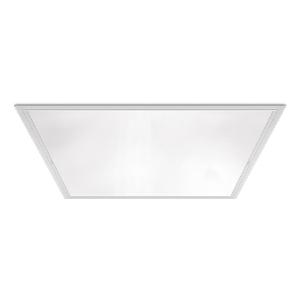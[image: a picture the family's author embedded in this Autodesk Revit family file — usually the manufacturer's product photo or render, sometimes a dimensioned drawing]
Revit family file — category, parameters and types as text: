
# Revit family: 3f_filippi_-_l_340_luce_diffusa_lgs_ip65v_3f_filippi_-_23972_-_l_340_25w-840_lgs_ip65v_596x596
name_source: partatom
category: Lighting Fixtures
units: mm (PartAtom-declared; Revit-internal decimal feet)

## family parameters
Cut with Voids When Loaded = No
Host = Face
Light Source = No
Part Type = Normal
Room Calculation Point = No
Round Connector Dimension = Use Diameter
Shared = No

## types (1)
- 3F Filippi - L 340 Luce Diffusa LGS IP65V (1 x LED, 3785 lm, 29 W, 4000 K)
    Apparent Load = 29 VA
    Approval mark = ENEC
    CIE Flux Codes = 67 92 98 100 100
    Color Rendering = 80
    Color Temperature = 4000 K
    Control Gear = Electronic ballast
    Default Elevation = 1800 mm
    Description = ILLUMINOTECHNICAL
Luminous efficiency 100% (DLOR 100%, ULOR 0%).
Initial luminous flux of the luminaire 3785 lm.
Direct symmetric distribution.
Installation Interdistance Transv.D = 1.19 x hu - Long.D = 1.17 x hu.
Average luminance <1500 cd/m² for radial angles >65°.
Tabular UGR (CIE 117 - 4H-8H; S=0.25H; 70/50/20): RUG 16.4 - 16.4.
Beam angle: 87° - 86°.
Luminous efficacy 131 lm/W.
Lifetime (L93/B10): 30000 h. (tq+25°C)
Lifetime (L90/B10): 50000 h. (tq+25°C)
Lifetime (L85/B10): 80000 h. (tq+25°C)
Lifetime (L80/B10): 100000 h. (tq+25°C)
Sudden decreased luminous flux after 50000 hours: 0% (C0).
Photobiological safety in compliance with IEC/TR 62778: RG0 risk exempt, (IEC 62471).
In compliance with IEC/EN 62722-2-1 - IEC/EN 62717 standards.

SOURCE
Squared LED module 25W/840.
Energy efficiency class (UE 2019/2020 - UE 2019/2015): C.
CIE 13.3 Colour rendering index: CRI >80 (R9 <50%).
IES TM-30 Fidelity Index: Rf = 84 Rg = 95.
CCT nominal colour temperature 4000 K.
Colour initial tolerance (MacAdam): SDCM 3.

MECHANICAL
Housing in hot-galvanised steel, painted in white polyester.
Perimetral frame in white polycarbonate.
LGS micro-prismatic flat diffuser in transparent methacrylate (PMMA), multi-lenticular exterior, anti-glare.
Anti-glare opal polycarbonate filter for brightness uniformity.
Luminaire with limited surface temperature. - D - (EN 60598-2-24)
Dimensions: 596x596 mm, height 80 mm. Weight 4.45 kg.
IP65 protection degree for exposed part, IP40 for recessed part.
Mechanical strength to impacts IK06 (1 joule).
Glow-wire test resistance 650°C.

ELECTRICAL
Wiring on a separate unit.
Halogen Free electronic wiring 230V-50/60Hz, power factor 0.95, THD <25%, constant output current, SELV, class II, 1 driver.
Power of the luminaire 29 W.
CE - IEC 60598-1 - EN 60598-1.
SAFE FLICKER: PstLM=<1 and SVM=<0.4 (IEC TR 61547-1 and IEC TR 63158), to ensure a more comfortable and safe light.
Luminaire compliant with EN 60598-2-22 for power supply from a centralised emergency system CPSS (Central Power Supply System), not incorporated in the luminaire - high risk areas excluded. The default power and flux are 100% in AC and 100% in DC.
Ambient temperature from 0°C to +40°C.
Temperature class T6 max 85°C.
Relative humidity UR: <85%.

INSTALLATION
Lay-on or pull-up recessed fitting using frame accessory.
All accessories dedicated to this product are available on the Catalog and on our website www.3F-Filippi.com.

APPLICATIONS
Suitable product for food production plants (HACCP), IFS (Food Version 6), BRC (GSFS Food Version 7).
In environments requiring protection and simplified cleaning.
Hospitals, pharmaceutical, chemical, aseptic laboratories, sterilised rooms.
Environments: with VDTs, meeting rooms, offices.
Environments: architectural, commercial, staterooms, banks.
Environments where demanding visual tasks are performed and soft diffuse light is required for optimal visual comfort and total shielding of the light source.

WARNING
Luminaire designed for disposal/recycling at end-of-life.
Replaceable (LED only) light source by a professional. Replaceable control gear by a professional.
    Height = 0 mm  [stored 0 ft]
    Lamp = 1 x LED
    Lamp Light Flux = 3785 lm
    Lamp Power = 29 W
    Lamp count = 1
    Length = 596 mm
    Lifetime = 50000 h
    Luminous efficacy = 131 lm/W
    Manufacturer = 3F Filippi
    ModVariant = No
    Model = 3F Filippi - 23972 - L 340 25W-840 LGS IP65V 596x596
    Mounting Place = Ceiling
    Mounting Type = Recessed
    Number of Poles = 1
    OnlyDefault = Yes
    Power Factor = 1
    Product Name = 3F Filippi - L 340 Luce Diffusa LGS IP65V
    Product group = recessed luminaire
    ProductGroupID = 4
    Protection Class = Protection class II
    Protection Degree = IP 40
    RLX_Detail_Level = 1
    RLX_Emergency_Light_Flux = 0 lm
    RLX_Emergency_Type = 0
    RLX_Emergency_Type_DB = No
    RlxData = <blob elided: 153657 chars, md5=776a8dae>
    Socket = socket
    Standby Power = 0 W
    System Light Flux = 3785 lm
    System Power = 29 W
    Type Comments = Product without accessories
    Type Image = 3ffilippi_l_340_luce_diffusa_lgs_ip65v.jpg
    URL = http://relux.com
    VarID = ---
    Voltage = 0 V
    Weight = 0.00 kg
    Width = 596 mm

note: [stored X ft] marks values corroborated as IEEE doubles in the binary element streams (Revit-internal decimal feet)

## geometry (parser evidence)
native form markers: Blend x4, Sweep x11
no freeform markers — native parametric forms only
